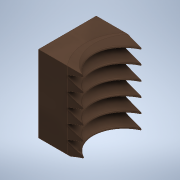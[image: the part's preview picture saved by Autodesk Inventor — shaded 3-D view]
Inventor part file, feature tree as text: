
AUTODESK INVENTOR PART (.ipt)
format: ipt  version: 2020 (Build 240168000, 168)  size: 395,264 bytes
history: native  units: in
note: dims shown in document units (in); Inventor stores cm internally (conversion verified against a paired STEP export)
features: sketch x3, extrude x2, hole x1, thread x1, revolve x1, helix x1, projected_geometry x1
ambient origin geometry x8: Origin, YZ Plane, XZ Plane, XY Plane, X Axis, Y Axis, Z Axis, Center Point
bodies: Solid3 (feature_tree)
feature tree (10):
  sketch  "Sketch2"  dims[d6=1.375in d7=0.5in d8=0.0in]
  extrude  "Extrusion2"  Depth=0.5in TaperAngle=0.0deg
  hole  "Hole1"  [1 undecoded]
  thread  "Thread1"  [1 undecoded]
  revolve  "Revolution1"  [1 undecoded]
  helix  "Coil1"  [1 undecoded]
  extrude  "Extrusion4"  Depth=0.091in
  projected_geometry  "Projected Loop1"
  sketch  "Sketch4"  dims[d9=0.565in d10=1.25in d11=0.375in d12=0.25in d13=0.5635in d14=1.528in d15=0.0in d16=0.1875in d17=0.1875in]
  sketch  "Sketch5"  dims[d20=0.5in d21=0.0in d22=0.3779in d23=0.0146in d24=0.0146in d27=0.0909in d29=0.3779in d31=0.0in d32=0.091in d33=0.6818in d34=0.3937in d35=0.0in d36=0.0in d37=0.0in d38=0.0in d39=0.0in d40=0.5in d41=0.0in d42=0.5in d43=0.0344in]
note: 4 required parameter values undecoded (feature->parameter linkage not recoverable at this tier; creation-order binding heuristic only, values carry confidence <= 0.55)